# Revit family: Sanitary_Toilets_hansgrohe_61176XXX-EluPura-Original-S-Floorstandin__00
name_source: partatom
category: Plumbing Fixtures
units: mm (PartAtom-declared; Revit-internal decimal feet)

## family parameters
Always vertical = No
Cut with Voids When Loaded = No
OmniClass Number = 23.31.19.00
OmniClass Title = Toilets
Part Type = Normal
Room Calculation Point = No
Round Connector Dimension = Use Diameter
Shared = No
Work Plane-Based = Yes

## types (1)
- 450 White
    Connector Description = Water Outlet 110 mm
    Default Elevation = 1219 mm
    Description = EluPura Original S Floorstanding WC close coupled 640 back to wall with horizontal/vertical outlet rimless AquaChannel Flush, SmartClean
    Diameter = 110 mm  [stored 0.360892 ft]
    Manufacturer = Hansgrohe
    Material = Hansgrohe - Ceramic - 450 White
    Model = 61176XXX
    Product Guid = 7a46471c-12ed-487e-88d7-56b64c42ac47
    Product Page URL = https://www.hansgrohe.com
    Product data url = https://bimobject.com
    URL = https://www.hansgrohe.com
    Version = 1

note: [stored X ft] marks values corroborated as IEEE doubles in the binary element streams (Revit-internal decimal feet)

## geometry (parser evidence)
native form markers: Sweep x3
no freeform markers — native parametric forms only
